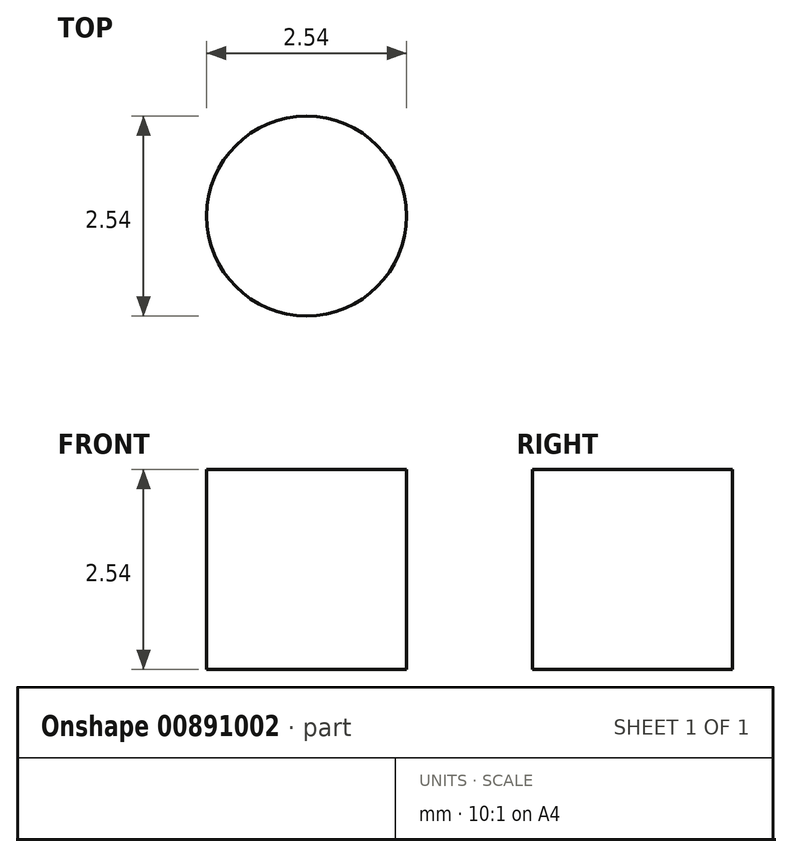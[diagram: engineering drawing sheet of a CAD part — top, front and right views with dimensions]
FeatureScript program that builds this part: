
annotation { "Feature Type Name" : "Feature", "Feature Type Description" : "" }
export const myFeature = defineFeature(function(context is Context, id is Id, definition is map)
    precondition{}
    {
        {
            var Q0;
            Q0=qCreatedBy(makeId("Top.planeOp"),FACE);
            var sketch = newSketch(context, id + "F0", { "sketchPlane" : qUnion([Q0])});
            skCircle(sketch, "E0", {"center": v(0, 0) * mm, "radius": 1.27 * mm});
            skSolve(sketch);
        }
        {
            var Q0;
            Q0 = qSketchRegion(id + "F0", true);
            extrude(context, id + "F1", {"entities" : qUnion([Q0]), "depth" : 2.54 * mm, "offsetDistance" : 25.4 * mm});
        }
    });
